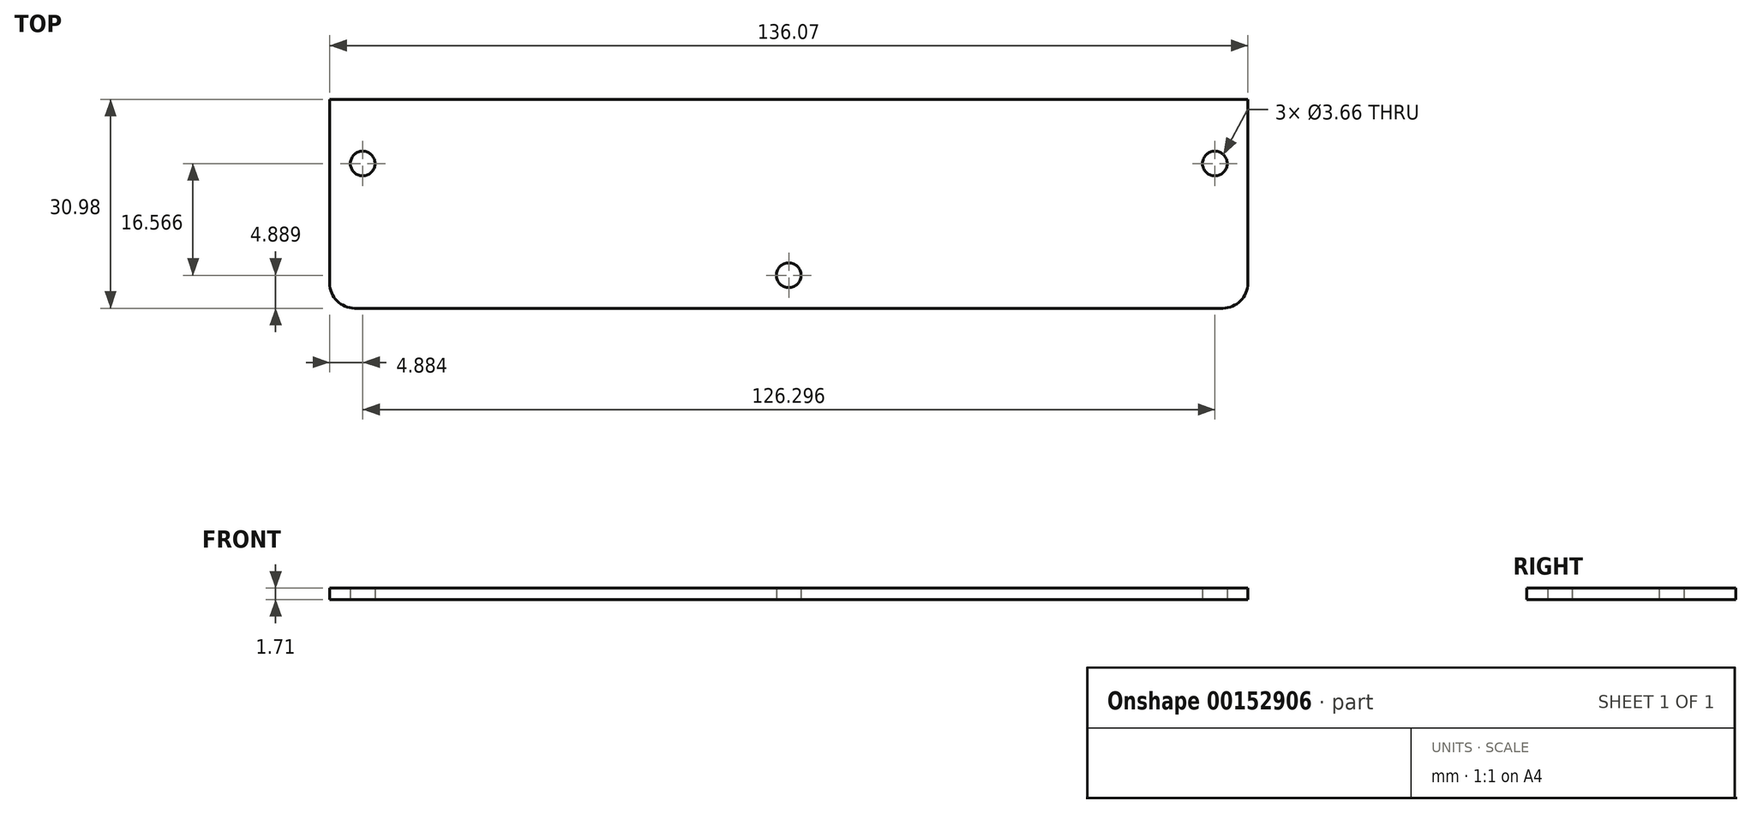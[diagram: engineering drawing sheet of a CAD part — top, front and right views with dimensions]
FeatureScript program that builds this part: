
annotation { "Feature Type Name" : "Feature", "Feature Type Description" : "" }
export const myFeature = defineFeature(function(context is Context, id is Id, definition is map)
    precondition{}
    {
        {
            var Q0;
            Q0=qCreatedBy(makeId("Top.planeOp"),FACE);
            var sketch = newSketch(context, id + "F0", { "sketchPlane" : qUnion([Q0])});
            skLineSegment(sketch, "E0.bottom", {"start": v(0, 0) * mm, "end": v(136.07, 0) * mm});
            skLineSegment(sketch, "E0.top", {"start": v(0, -30.98) * mm, "end": v(136.07, -30.98) * mm});
            skLineSegment(sketch, "E0.left", {"start": v(0, 0) * mm, "end": v(0, -30.98) * mm});
            skLineSegment(sketch, "E0.right", {"start": v(136.07, 0) * mm, "end": v(136.07, -30.98) * mm});
            skLineSegment(sketch, "E1", {"start": v(0, -9.53) * mm, "end": v(4.88, -9.53) * mm, "construction": true});
            skLineSegment(sketch, "E2", {"start": v(4.88, -9.53) * mm, "end": v(4.88, 0) * mm, "construction": true});
            skLineSegment(sketch, "E3", {"start": v(131.18, 0) * mm, "end": v(131.18, -9.53) * mm, "construction": true});
            skLineSegment(sketch, "E4", {"start": v(131.18, -9.52) * mm, "end": v(136.07, -9.52) * mm, "construction": true});
            skLineSegment(sketch, "E5", {"start": v(68.03, -30.98) * mm, "end": v(68.03, -26.1) * mm, "construction": true});
            skCircle(sketch, "E6", {"center": v(4.88, -9.53) * mm, "radius": 1.83 * mm});
            skCircle(sketch, "E7", {"center": v(131.18, -9.53) * mm, "radius": 1.83 * mm});
            skCircle(sketch, "E8", {"center": v(68.03, -26.1) * mm, "radius": 1.83 * mm});
            skSolve(sketch);
        }
        {
            var Q0;
            Q0=qSketchRegion(id+"F0",true);
            extrude(context, id + "F1", {"entities" : qUnion([Q0]), "depth" : 1.7 * mm});
        }
        {
            var Q0;
            Q0=makeQuery(id+"F1.opExtrude","SWEPT_EDGE",EDGE,{"disambiguationData":[OSD([sQuery(id+"F0.wireOp",EDGE,"E0.top"),sQuery(id+"F0.wireOp",EDGE,"E0.left")])]});
            var Q1;
            Q1=makeQuery(id+"F1.opExtrude","SWEPT_EDGE",EDGE,{"disambiguationData":[OSD([sQuery(id+"F0.wireOp",EDGE,"E0.top"),sQuery(id+"F0.wireOp",EDGE,"E0.right")])]});
            fillet(context, id + "F2", {"entities" : qUnion([Q0, Q1]), "radius" : 3.7 * mm, "tangentPropagation" : true, "allowEdgeOverflow" : false});
        }
    });
